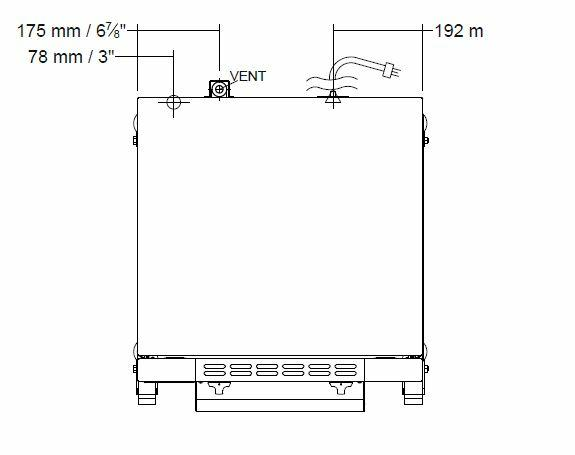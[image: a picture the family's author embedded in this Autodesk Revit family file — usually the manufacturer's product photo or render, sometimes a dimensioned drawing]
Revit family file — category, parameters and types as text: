
# Revit family: QF_MOFFAT_E27D3-2_NZ
name_source: partatom
category: Specialty Equipment
revit_build: Autodesk Revit 2014 (Build: 20130308_1515(x64)
units: mm (PartAtom-declared; Revit-internal decimal feet)

## types (1)
- QF_MOFFAT_E27D3-2_NZ
    Apparent Power = 4508 VA
    Cold Water Connection Height = 0 mm  [stored 0 ft]
    Cold Water Flow = 0 GPM
    Cold Water Maximum Pressure = 80.00 psi
    Cold Water Minimum Pressure = 20.00 psi
    Cold Water RI Height = 0 mm  [stored 0 ft]
    Cold Water Size = 1"
    Cold Water Temperature Recommended = 0 °F
    Conn Conduit = Yes
    Cycle = 50 Hz
    Depth = 762 mm  [stored 2.5 ft]
    Description = FULL SIZE DIGITAL / ELECTRIC CONVECTION OVENS DOUBLE STACKED ON A STAINLESS STEEL BASE STAND
    Elec Conn Connection Height = 0 mm  [stored 0 ft]
    Elec Conn RI Height = 0 mm  [stored 0 ft]
    Electrical Remarks = 230-240V, 50Hz, 1P+N+E 4.7kW, 19.6A
    Exhaust RI Height = 0 mm  [stored 0 ft]
    Exhaust Static Press = 0.00 in-wg
    Exhaust Vent Depth = 0 mm  [stored 0 ft]
    Exhaust Vent Diameter = 0 mm  [stored 0 ft]
    Exhaust Vent Width = 0 mm  [stored 0 ft]
    Exhaust Volume = 0 CFM
    FL Amps = 20 A
    Foodservice Equipment Identifier = Yes
    Height = 1571 mm  [stored 5.1542 ft]
    Height of Stand = 454 mm  [stored 1.4895 ft]
    Identify Quantity as Lot = Yes
    Length = 810 mm  [stored 2.65748 ft]
    Manufacturer = MOFFAT
    Max Overcurrent Protection = 0 A
    Min Ckt Ampacity = 0 A
    Model = E27D3-2
    Number of Poles = 1
    Phase = 1
    URL = www.moffat.com.au
    URL Cutsheet = www.moffat.com.au
    Volts = 230 V
    Watts = 4700 W
    Weight in Pounds = 0

note: [stored X ft] marks values corroborated as IEEE doubles in the binary element streams (Revit-internal decimal feet)

## geometry (parser evidence)
native form markers: Blend x16, Sweep x9
no freeform markers — native parametric forms only
